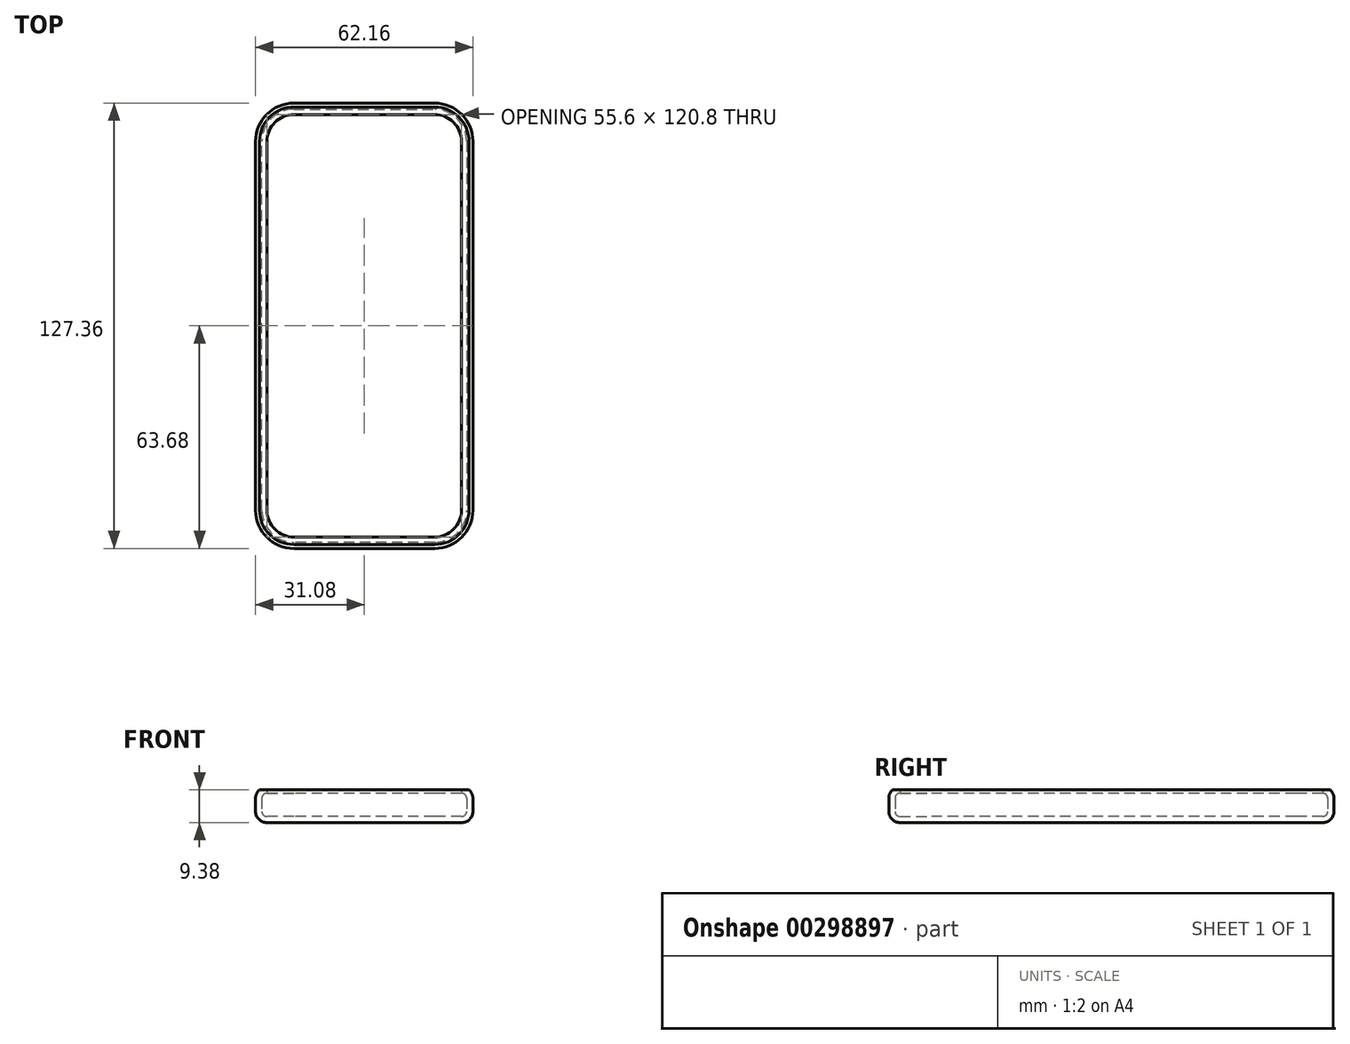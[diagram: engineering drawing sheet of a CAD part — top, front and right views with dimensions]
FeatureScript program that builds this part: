
annotation { "Feature Type Name" : "Feature", "Feature Type Description" : "" }
export const myFeature = defineFeature(function(context is Context, id is Id, definition is map)
    precondition{}
    {
        {
            var Q0;
            Q0=qCreatedBy(makeId("Top.planeOp"),FACE);
            var sketch = newSketch(context, id + "F0", { "sketchPlane" : qUnion([Q0])});
            skLineSegment(sketch, "E0.bottom", {"start": v(-32.5, 66) * mm, "end": v(32.5, 66) * mm});
            skLineSegment(sketch, "E0.top", {"start": v(-32.5, -66) * mm, "end": v(32.5, -66) * mm});
            skLineSegment(sketch, "E0.left", {"start": v(-32.5, 66) * mm, "end": v(-32.5, -66) * mm});
            skLineSegment(sketch, "E0.right", {"start": v(32.5, 66) * mm, "end": v(32.5, -66) * mm});
            skPoint(sketch, "E0.middle", {"position": v(0, 0) * mm});
            skSolve(sketch);
        }
        {
            var Q0;
            Q0 = qSketchRegion(id + "F0", true);
            extrude(context, id + "F1", {"entities" : qUnion([Q0]), "depth" : 9.6 * mm});
        }
        {
            var Q0;
            Q0=makeQuery(id+"F1.opExtrude","CAP_FACE",FACE,{"disambiguationData":[OSD([sQuery(id+"F0.wireOp",EDGE,"E0.bottom"),sQuery(id+"F0.wireOp",EDGE,"E0.top"),sQuery(id+"F0.wireOp",EDGE,"E0.left"),sQuery(id+"F0.wireOp",EDGE,"E0.right")])],"isStart":false});
            var sketch = newSketch(context, id + "F2", { "sketchPlane" : qUnion([Q0])});
            skLineSegment(sketch, "E1.bottom", {"start": v(-20.14, 61.9) * mm, "end": v(20.14, 61.9) * mm});
            skLineSegment(sketch, "E1.top", {"start": v(-20.14, -61.9) * mm, "end": v(20.14, -61.9) * mm});
            skLineSegment(sketch, "E1.left", {"start": v(-29.3, 52.74) * mm, "end": v(-29.3, -52.74) * mm});
            skLineSegment(sketch, "E1.right", {"start": v(29.3, 52.74) * mm, "end": v(29.3, -52.74) * mm});
            skPoint(sketch, "E1.middle", {"position": v(0, 0) * mm});
            skPoint(sketch, "E2.visualSharp", {"position": v(-29.3, 61.9) * mm});
            skArc(sketch, "E2.filletArc", {"start": v(-20.14, 61.9) * mm, "mid": v(-26.62, 59.22) * mm, "end": v(-29.3, 52.74) * mm});
            skPoint(sketch, "E3.visualSharp", {"position": v(29.3, 61.9) * mm});
            skArc(sketch, "E3.filletArc", {"start": v(29.3, 52.74) * mm, "mid": v(26.62, 59.22) * mm, "end": v(20.14, 61.9) * mm});
            skPoint(sketch, "E4.visualSharp", {"position": v(29.3, -61.9) * mm});
            skArc(sketch, "E4.filletArc", {"start": v(20.14, -61.9) * mm, "mid": v(26.62, -59.22) * mm, "end": v(29.3, -52.74) * mm});
            skPoint(sketch, "E5.visualSharp", {"position": v(-29.3, -61.9) * mm});
            skArc(sketch, "E5.filletArc", {"start": v(-29.3, -52.74) * mm, "mid": v(-26.62, -59.22) * mm, "end": v(-20.14, -61.9) * mm});
            skSolve(sketch);
        }
        {
            var Q0;
            Q0=sQuery(id+"F2.wireOp",VERTEX,"E1.left.end");
            var Q1;
            Q1=sQuery(id+"F2.wireOp",EDGE,"E1.left");
            cPlane(context, id + "F3", {"entities" : qUnion([Q0, Q1]), "cplaneType" : CPlaneType.CURVE_POINT, "offset" : 25 * mm, "width" : 150 * mm, "height" : 150 * mm});
        }
        {
            var Q0;
            Q0=qCreatedBy(id+"F3.planeOp",FACE);
            var sketch = newSketch(context, id + "F4", { "sketchPlane" : qUnion([Q0])});
            skPoint(sketch, "E6.visualSharp", {"position": v(-29.3, 9.6) * mm});
            skLineSegment(sketch, "E7.right", {"start": v(-27.8, 9.6) * mm, "end": v(-27.8, 8.6) * mm});
            skLineSegment(sketch, "E8.bottom", {"start": v(-27.8, 8.6) * mm, "end": v(-27.86, 8.6) * mm});
            skLineSegment(sketch, "E8.top", {"start": v(-27.8, 2) * mm, "end": v(-27.86, 2) * mm});
            skLineSegment(sketch, "E8.left", {"start": v(-27.8, 8.6) * mm, "end": v(-27.8, 2) * mm});
            skLineSegment(sketch, "E8.right", {"start": v(-29.3, 7.16) * mm, "end": v(-29.3, 3.44) * mm});
            skPoint(sketch, "E9.visualSharp", {"position": v(-29.3, 8.6) * mm});
            skArc(sketch, "E9.filletArc", {"start": v(-27.86, 8.6) * mm, "mid": v(-28.88, 8.18) * mm, "end": v(-29.3, 7.16) * mm});
            skPoint(sketch, "E10.visualSharp", {"position": v(-29.3, 2) * mm});
            skArc(sketch, "E10.filletArc", {"start": v(-29.3, 3.44) * mm, "mid": v(-28.88, 2.42) * mm, "end": v(-27.86, 2) * mm});
            skLineSegment(sketch, "E11.bottom", {"start": v(-27.8, 9.6) * mm, "end": v(-26.55, 9.6) * mm});
            skLineSegment(sketch, "E11.top", {"start": v(-27.8, 2) * mm, "end": v(-26.55, 2) * mm});
            skLineSegment(sketch, "E11.left", {"start": v(-27.8, 9.6) * mm, "end": v(-27.8, 2) * mm});
            skLineSegment(sketch, "E11.right", {"start": v(-26.55, 9.6) * mm, "end": v(-26.55, 2) * mm});
            skLineSegment(sketch, "E12", {"start": v(-29.3, 8.6) * mm, "end": v(-29.3, 9.6) * mm});
            skSolve(sketch);
        }
        {
            var Q0;
            Q0 = qSketchRegion(id + "F4", true);
            var Q1;
            Q1 = qConstructionFilter(qBodyType(qCreatedBy(id + "F2" ,EDGE), BodyType.WIRE), ConstructionObject.NO);
            sweep(context, id + "F5", {"operationType" : NewBodyOperationType.REMOVE, "profiles" : qUnion([Q0]), "path" : qUnion([Q1])});
        }
        {
            var Q0;
            {var subQ0=sQuery(id+"F4.wireOp",EDGE,"XylM6zGY-3X4m-RJua-ZG8b-0BQECrTlgpck.right");Q0=makeQuery(id+"F5.boolean.opBoolean","SPLIT",FACE,{"disambiguationData":[TD([makeQuery(id+"F5.opSweep","SWEPT_FACE",FACE,{"disambiguationData":[OSD([sQuery(id+"F2.wireOp",EDGE,"E1.bottom"),subQ0])]})])],"derivedFrom":makeQuery(id+"F1.opExtrude","CAP_FACE",FACE,{"disambiguationData":[OSD([sQuery(id+"F0.wireOp",EDGE,"E0.bottom"),sQuery(id+"F0.wireOp",EDGE,"E0.top"),sQuery(id+"F0.wireOp",EDGE,"E0.left"),sQuery(id+"F0.wireOp",EDGE,"E0.right")])],"isStart":false})});}
            extrude(context, id + "F6", {"entities" : qUnion([Q0]), "operationType" : NewBodyOperationType.REMOVE, "oppositeDirection" : true, "depth" : 7.6 * mm});
        }
        {
            var Q0;
            Q0=makeQuery(id+"F1.opExtrude","CAP_FACE",FACE,{"disambiguationData":[OSD([sQuery(id+"F0.wireOp",EDGE,"E0.bottom"),sQuery(id+"F0.wireOp",EDGE,"E0.top"),sQuery(id+"F0.wireOp",EDGE,"E0.left"),sQuery(id+"F0.wireOp",EDGE,"E0.right")])],"isStart":true});
            var Q1;
            Q1=makeQuery(id+"F1.opExtrude","SWEPT_FACE",FACE,{"disambiguationData":[OSD([sQuery(id+"F0.wireOp",EDGE,"E0.top")])]});
            var Q2;
            Q2=makeQuery(id+"F1.opExtrude","SWEPT_FACE",FACE,{"disambiguationData":[OSD([sQuery(id+"F0.wireOp",EDGE,"E0.left")])]});
            var Q3;
            Q3=makeQuery(id+"F1.opExtrude","SWEPT_FACE",FACE,{"disambiguationData":[OSD([sQuery(id+"F0.wireOp",EDGE,"E0.bottom")])]});
            var Q4;
            Q4=makeQuery(id+"F1.opExtrude","SWEPT_FACE",FACE,{"disambiguationData":[OSD([sQuery(id+"F0.wireOp",EDGE,"E0.right")])]});
            var Q5;
            {var subQ1=sQuery(id+"F0.wireOp",EDGE,"E0.right");var subQ2=sQuery(id+"F0.wireOp",EDGE,"E0.bottom");var subQ3=sQuery(id+"F0.wireOp",EDGE,"E0.top");var subQ4=sQuery(id+"F0.wireOp",EDGE,"E0.left");Q5=makeQuery(id+"F5.boolean.opBoolean","SPLIT",FACE,{"disambiguationData":[TD([makeQuery(id+"F1.opExtrude","SWEPT_FACE",FACE,{"disambiguationData":[OSD([subQ2])]})])],"derivedFrom":makeQuery(id+"F1.opExtrude","CAP_FACE",FACE,{"disambiguationData":[OSD([subQ2,subQ3,subQ4,subQ1])],"isStart":false})});}
            shell(context, id + "F7", {"entities" : qUnion([Q0, Q1, Q2, Q3, Q4, Q5]), "thickness" : 1.78 * mm});
        }
    });
